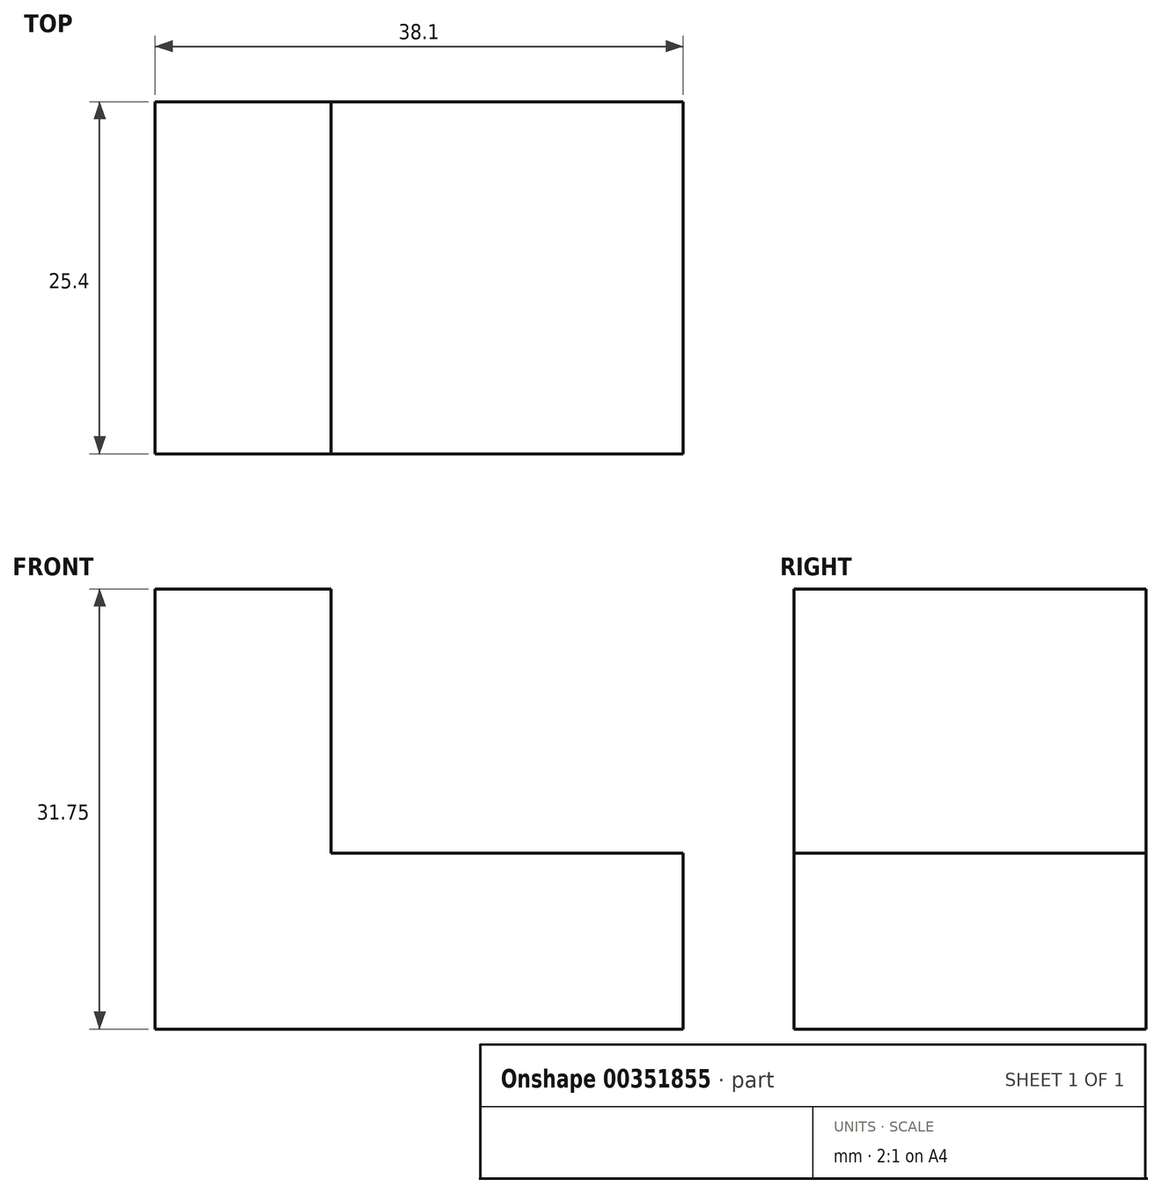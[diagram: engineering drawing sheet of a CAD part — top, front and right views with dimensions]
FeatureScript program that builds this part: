
annotation { "Feature Type Name" : "Feature", "Feature Type Description" : "" }
export const myFeature = defineFeature(function(context is Context, id is Id, definition is map)
    precondition{}
    {
        {
            var Q0;
            Q0=qCreatedBy(makeId("Front.planeOp"),FACE);
            var sketch = newSketch(context, id + "F0", { "sketchPlane" : qUnion([Q0])});
            skLineSegment(sketch, "E0", {"start": v(0, 0) * mm, "end": v(38.1, 0) * mm});
            skLineSegment(sketch, "E1", {"start": v(38.1, 0) * mm, "end": v(38.1, 12.7) * mm});
            skLineSegment(sketch, "E2", {"start": v(38.1, 12.7) * mm, "end": v(12.7, 12.7) * mm});
            skLineSegment(sketch, "E3", {"start": v(12.7, 12.7) * mm, "end": v(12.7, 31.75) * mm});
            skLineSegment(sketch, "E4", {"start": v(12.7, 31.75) * mm, "end": v(0, 31.75) * mm});
            skLineSegment(sketch, "E5", {"start": v(0, 31.75) * mm, "end": v(0, 0) * mm});
            skSolve(sketch);
        }
        {
            var Q0;
            Q0=makeQuery(id+"F0.imprint","IMPRINT",FACE,{"disambiguationData":[TD([[makeQuery(id+"F0.imprint","IMPRINT",EDGE,{"derivedFrom":sQuery(id+"F0.wireOp",EDGE,"E0")}),1.0]])]});
            extrude(context, id + "F1", {"entities" : qUnion([Q0]), "depth" : 25.4 * mm});
        }
    });
